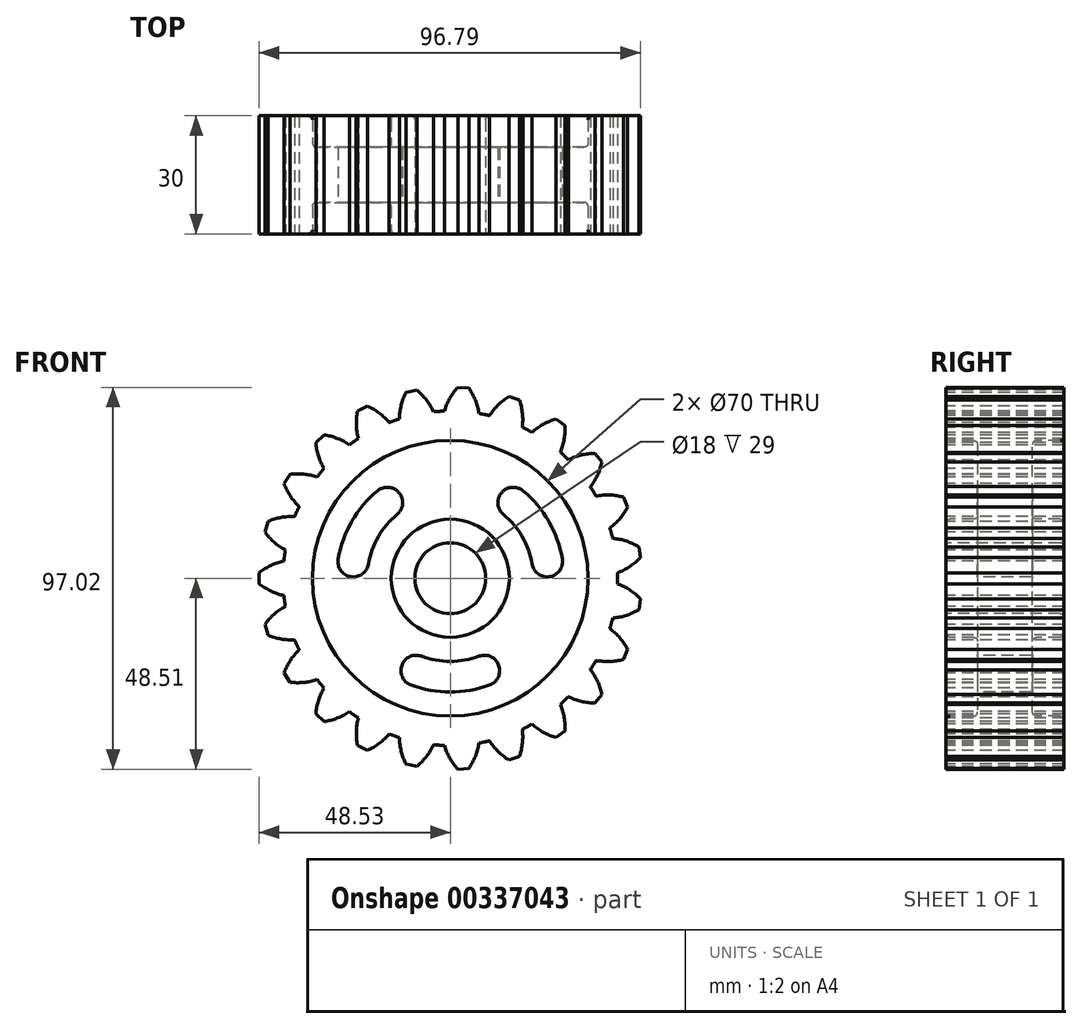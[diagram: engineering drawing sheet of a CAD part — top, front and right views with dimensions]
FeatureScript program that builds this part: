
annotation { "Feature Type Name" : "Feature", "Feature Type Description" : "" }
export const myFeature = defineFeature(function(context is Context, id is Id, definition is map)
    precondition{}
    {
        {
            var Q0;
            Q0=qCreatedBy(makeId("Right.planeOp"),FACE);
            var sketch = newSketch(context, id + "F0", { "sketchPlane" : qUnion([Q0])});
            skLineSegment(sketch, "E0", {"start": v(-15, 0) * mm, "end": v(15, 0) * mm});
            skLineSegment(sketch, "E1", {"start": v(15, 0) * mm, "end": v(15, 15) * mm});
            skLineSegment(sketch, "E2", {"start": v(15, 15) * mm, "end": v(7, 15) * mm});
            skLineSegment(sketch, "E3", {"start": v(7, 15) * mm, "end": v(7, 35) * mm});
            skLineSegment(sketch, "E4", {"start": v(7, 35) * mm, "end": v(15, 35) * mm});
            skLineSegment(sketch, "E5", {"start": v(15, 35) * mm, "end": v(15, 42.5) * mm});
            skLineSegment(sketch, "E6", {"start": v(15, 42.5) * mm, "end": v(-15, 42.5) * mm});
            skLineSegment(sketch, "E7", {"start": v(-15, 42.5) * mm, "end": v(-15, 35) * mm});
            skLineSegment(sketch, "E8", {"start": v(-15, 35) * mm, "end": v(-7, 35) * mm});
            skLineSegment(sketch, "E9", {"start": v(-7, 35) * mm, "end": v(-7, 15) * mm});
            skLineSegment(sketch, "E10", {"start": v(-7, 15) * mm, "end": v(-15, 15) * mm});
            skLineSegment(sketch, "E11", {"start": v(-15, 15) * mm, "end": v(-15, 0) * mm});
            skSolve(sketch);
        }
        {
            var Q0;
            Q0=makeQuery(id+"F0.imprint","IMPRINT",FACE,{"disambiguationData":[TD([[makeQuery(id+"F0.imprint","IMPRINT",EDGE,{"derivedFrom":sQuery(id+"F0.wireOp",EDGE,"E0")}),1.0]])]});
            var Q1;
            Q1=sQuery(id+"F0.wireOp",EDGE,"E0");
            revolve(context, id + "F1", {"entities" : qUnion([Q0]), "axis" : qUnion([Q1]), "revolveType" : RevolveType.FULL});
        }
        {
            var Q0;
            Q0=makeQuery(id+"F1.opRevolve","SWEPT_FACE",FACE,{"disambiguationData":[OSD([sQuery(id+"F0.wireOp",EDGE,"E11")])]});
            var sketch = newSketch(context, id + "F2", { "sketchPlane" : qUnion([Q0])});
            skCircle(sketch, "E12", {"center": v(0, 0) * mm, "radius": 9 * mm});
            skSolve(sketch);
        }
        {
            var Q0;
            Q0=makeQuery(id+"F2.imprint","IMPRINT",FACE,{"disambiguationData":[TD([[makeQuery(id+"F2.imprint","IMPRINT",EDGE,{"derivedFrom":sQuery(id+"F2.wireOp",EDGE,"E12")}),1.0]])]});
            extrude(context, id + "F3", {"entities" : qUnion([Q0]), "operationType" : NewBodyOperationType.REMOVE, "oppositeDirection" : true, "depth" : 35.8 * mm});
        }
        {
            var Q0;
            Q0=makeQuery(id+"F1.opRevolve","SWEPT_FACE",FACE,{"disambiguationData":[OSD([sQuery(id+"F0.wireOp",EDGE,"E7")])]});
            var sketch = newSketch(context, id + "F4", { "sketchPlane" : qUnion([Q0])});
            skLineSegment(sketch, "E13", {"start": v(0, 0) * mm, "end": v(-48.53, 0) * mm, "construction": true});
            skLineSegment(sketch, "E14", {"start": v(-48.53, 0) * mm, "end": v(-48.53, 1.4) * mm});
            skArc(sketch, "E15", {"start": v(-42.27, 4.4) * mm, "mid": v(-45.57, 3.27) * mm, "end": v(-48.53, 1.4) * mm});
            skLineSegment(sketch, "E16.MirrorCS", {"start": v(-48.53, 0) * mm, "end": v(-48.53, -1.4) * mm});
            skArc(sketch, "E17.MirrorCS", {"start": v(-42.27, -4.4) * mm, "mid": v(-45.57, -3.27) * mm, "end": v(-48.53, -1.4) * mm});
            skLineSegment(sketch, "E18.1.0", {"start": v(-46.73, -13.1) * mm, "end": v(-47.1, -11.74) * mm});
            skArc(sketch, "E18.1.1", {"start": v(-41.9, -7.17) * mm, "mid": v(-44.77, -9.15) * mm, "end": v(-47.1, -11.74) * mm});
            skLineSegment(sketch, "E18.1.2", {"start": v(-46.73, -13.1) * mm, "end": v(-46.35, -14.44) * mm});
            skArc(sketch, "E18.1.3", {"start": v(-39.52, -15.64) * mm, "mid": v(-43, -15.44) * mm, "end": v(-46.35, -14.44) * mm});
            skLineSegment(sketch, "E18.2.0", {"start": v(-41.46, -25.21) * mm, "end": v(-42.19, -24.02) * mm});
            skArc(sketch, "E18.2.1", {"start": v(-38.4, -18.2) * mm, "mid": v(-40.64, -20.89) * mm, "end": v(-42.19, -24.02) * mm});
            skLineSegment(sketch, "E18.2.2", {"start": v(-41.46, -25.21) * mm, "end": v(-40.73, -26.4) * mm});
            skArc(sketch, "E18.2.3", {"start": v(-33.83, -25.72) * mm, "mid": v(-37.24, -26.47) * mm, "end": v(-40.73, -26.4) * mm});
            skLineSegment(sketch, "E18.3.0", {"start": v(-33.12, -35.46) * mm, "end": v(-34.14, -34.5) * mm});
            skArc(sketch, "E18.3.1", {"start": v(-32.07, -27.9) * mm, "mid": v(-33.5, -31.08) * mm, "end": v(-34.14, -34.5) * mm});
            skLineSegment(sketch, "E18.3.2", {"start": v(-33.12, -35.46) * mm, "end": v(-32.1, -36.42) * mm});
            skArc(sketch, "E18.3.3", {"start": v(-25.64, -33.9) * mm, "mid": v(-28.72, -35.54) * mm, "end": v(-32.1, -36.42) * mm});
            skLineSegment(sketch, "E18.4.0", {"start": v(-22.33, -43.09) * mm, "end": v(-23.57, -42.44) * mm});
            skArc(sketch, "E18.4.1", {"start": v(-23.35, -35.5) * mm, "mid": v(-23.87, -38.96) * mm, "end": v(-23.57, -42.44) * mm});
            skLineSegment(sketch, "E18.4.2", {"start": v(-22.33, -43.09) * mm, "end": v(-21.08, -43.73) * mm});
            skArc(sketch, "E18.4.3", {"start": v(-15.54, -39.56) * mm, "mid": v(-18.07, -41.97) * mm, "end": v(-21.08, -43.73) * mm});
            skLineSegment(sketch, "E18.5.0", {"start": v(-9.87, -47.51) * mm, "end": v(-11.24, -47.23) * mm});
            skArc(sketch, "E18.5.1", {"start": v(-12.9, -40.5) * mm, "mid": v(-12.47, -43.96) * mm, "end": v(-11.24, -47.23) * mm});
            skLineSegment(sketch, "E18.5.2", {"start": v(-9.87, -47.51) * mm, "end": v(-8.5, -47.8) * mm});
            skArc(sketch, "E18.5.3", {"start": v(-4.3, -42.28) * mm, "mid": v(-6.07, -45.29) * mm, "end": v(-8.5, -47.8) * mm});
            skLineSegment(sketch, "E18.6.0", {"start": v(3.31, -48.41) * mm, "end": v(1.91, -48.5) * mm});
            skArc(sketch, "E18.6.1", {"start": v(-1.5, -42.47) * mm, "mid": v(-0.15, -45.7) * mm, "end": v(1.91, -48.5) * mm});
            skLineSegment(sketch, "E18.6.2", {"start": v(3.31, -48.41) * mm, "end": v(4.7, -48.32) * mm});
            skArc(sketch, "E18.6.3", {"start": v(7.27, -41.87) * mm, "mid": v(6.37, -45.25) * mm, "end": v(4.7, -48.32) * mm});
            skLineSegment(sketch, "E18.7.0", {"start": v(16.25, -45.72) * mm, "end": v(14.93, -46.2) * mm});
            skArc(sketch, "E18.7.1", {"start": v(10, -41.3) * mm, "mid": v(12.18, -44.04) * mm, "end": v(14.93, -46.2) * mm});
            skLineSegment(sketch, "E18.7.2", {"start": v(16.25, -45.72) * mm, "end": v(17.57, -45.26) * mm});
            skArc(sketch, "E18.7.3", {"start": v(18.3, -38.36) * mm, "mid": v(18.34, -41.85) * mm, "end": v(17.57, -45.26) * mm});
            skLineSegment(sketch, "E18.8.0", {"start": v(27.98, -39.64) * mm, "end": v(26.84, -40.45) * mm});
            skArc(sketch, "E18.8.1", {"start": v(20.78, -37.07) * mm, "mid": v(23.61, -39.12) * mm, "end": v(26.84, -40.45) * mm});
            skLineSegment(sketch, "E18.8.2", {"start": v(27.98, -39.64) * mm, "end": v(29.13, -38.84) * mm});
            skArc(sketch, "E18.8.3", {"start": v(27.97, -32) * mm, "mid": v(28.95, -35.35) * mm, "end": v(29.13, -38.84) * mm});
            skLineSegment(sketch, "E18.9.0", {"start": v(37.64, -30.62) * mm, "end": v(36.76, -31.71) * mm});
            skArc(sketch, "E18.9.1", {"start": v(30.01, -30.1) * mm, "mid": v(33.3, -31.3) * mm, "end": v(36.76, -31.71) * mm});
            skLineSegment(sketch, "E18.9.2", {"start": v(37.64, -30.62) * mm, "end": v(38.53, -29.54) * mm});
            skArc(sketch, "E18.9.3", {"start": v(35.57, -23.26) * mm, "mid": v(37.41, -26.23) * mm, "end": v(38.53, -29.54) * mm});
            skLineSegment(sketch, "E18.10.0", {"start": v(44.5, -19.33) * mm, "end": v(43.95, -20.62) * mm});
            skArc(sketch, "E18.10.1", {"start": v(37.02, -20.88) * mm, "mid": v(40.5, -21.15) * mm, "end": v(43.95, -20.62) * mm});
            skLineSegment(sketch, "E18.10.2", {"start": v(44.5, -19.33) * mm, "end": v(45.07, -18.05) * mm});
            skArc(sketch, "E18.10.3", {"start": v(40.52, -12.8) * mm, "mid": v(43.1, -15.16) * mm, "end": v(45.07, -18.05) * mm});
            skLineSegment(sketch, "E18.11.0", {"start": v(48.07, -6.6) * mm, "end": v(47.88, -8) * mm});
            skArc(sketch, "E18.11.1", {"start": v(41.28, -10.12) * mm, "mid": v(44.7, -9.44) * mm, "end": v(47.88, -8) * mm});
            skLineSegment(sketch, "E18.11.2", {"start": v(48.07, -6.6) * mm, "end": v(48.26, -5.22) * mm});
            skArc(sketch, "E18.11.3", {"start": v(42.48, -1.4) * mm, "mid": v(45.6, -2.97) * mm, "end": v(48.26, -5.22) * mm});
            skLineSegment(sketch, "E18.12.0", {"start": v(48.07, 6.6) * mm, "end": v(48.26, 5.22) * mm});
            skArc(sketch, "E18.12.1", {"start": v(42.48, 1.4) * mm, "mid": v(45.6, 2.97) * mm, "end": v(48.26, 5.22) * mm});
            skLineSegment(sketch, "E18.12.2", {"start": v(48.07, 6.6) * mm, "end": v(47.88, 8) * mm});
            skArc(sketch, "E18.12.3", {"start": v(41.28, 10.12) * mm, "mid": v(44.7, 9.44) * mm, "end": v(47.88, 8) * mm});
            skLineSegment(sketch, "E18.13.0", {"start": v(44.5, 19.33) * mm, "end": v(45.07, 18.05) * mm});
            skArc(sketch, "E18.13.1", {"start": v(40.52, 12.8) * mm, "mid": v(43.1, 15.16) * mm, "end": v(45.07, 18.05) * mm});
            skLineSegment(sketch, "E18.13.2", {"start": v(44.5, 19.33) * mm, "end": v(43.95, 20.62) * mm});
            skArc(sketch, "E18.13.3", {"start": v(37.02, 20.88) * mm, "mid": v(40.5, 21.15) * mm, "end": v(43.95, 20.62) * mm});
            skLineSegment(sketch, "E18.14.0", {"start": v(37.64, 30.62) * mm, "end": v(38.53, 29.54) * mm});
            skArc(sketch, "E18.14.1", {"start": v(35.57, 23.26) * mm, "mid": v(37.41, 26.23) * mm, "end": v(38.53, 29.54) * mm});
            skLineSegment(sketch, "E18.14.2", {"start": v(37.64, 30.62) * mm, "end": v(36.76, 31.71) * mm});
            skArc(sketch, "E18.14.3", {"start": v(30.01, 30.1) * mm, "mid": v(33.3, 31.3) * mm, "end": v(36.76, 31.71) * mm});
            skLineSegment(sketch, "E18.15.0", {"start": v(27.98, 39.64) * mm, "end": v(29.13, 38.84) * mm});
            skArc(sketch, "E18.15.1", {"start": v(27.97, 32) * mm, "mid": v(28.95, 35.35) * mm, "end": v(29.13, 38.84) * mm});
            skLineSegment(sketch, "E18.15.2", {"start": v(27.98, 39.64) * mm, "end": v(26.84, 40.45) * mm});
            skArc(sketch, "E18.15.3", {"start": v(20.78, 37.07) * mm, "mid": v(23.61, 39.12) * mm, "end": v(26.84, 40.45) * mm});
            skLineSegment(sketch, "E18.16.0", {"start": v(16.25, 45.72) * mm, "end": v(17.57, 45.26) * mm});
            skArc(sketch, "E18.16.1", {"start": v(18.3, 38.36) * mm, "mid": v(18.34, 41.85) * mm, "end": v(17.57, 45.26) * mm});
            skLineSegment(sketch, "E18.16.2", {"start": v(16.25, 45.72) * mm, "end": v(14.93, 46.2) * mm});
            skArc(sketch, "E18.16.3", {"start": v(10, 41.3) * mm, "mid": v(12.18, 44.04) * mm, "end": v(14.93, 46.2) * mm});
            skLineSegment(sketch, "E18.17.0", {"start": v(3.31, 48.41) * mm, "end": v(4.7, 48.32) * mm});
            skArc(sketch, "E18.17.1", {"start": v(7.27, 41.87) * mm, "mid": v(6.37, 45.25) * mm, "end": v(4.7, 48.32) * mm});
            skLineSegment(sketch, "E18.17.2", {"start": v(3.31, 48.41) * mm, "end": v(1.91, 48.5) * mm});
            skArc(sketch, "E18.17.3", {"start": v(-1.5, 42.47) * mm, "mid": v(-0.15, 45.7) * mm, "end": v(1.91, 48.5) * mm});
            skLineSegment(sketch, "E18.18.0", {"start": v(-9.87, 47.51) * mm, "end": v(-8.5, 47.8) * mm});
            skArc(sketch, "E18.18.1", {"start": v(-4.3, 42.28) * mm, "mid": v(-6.07, 45.29) * mm, "end": v(-8.5, 47.8) * mm});
            skLineSegment(sketch, "E18.18.2", {"start": v(-9.87, 47.51) * mm, "end": v(-11.24, 47.23) * mm});
            skArc(sketch, "E18.18.3", {"start": v(-12.9, 40.5) * mm, "mid": v(-12.47, 43.96) * mm, "end": v(-11.24, 47.23) * mm});
            skLineSegment(sketch, "E18.19.0", {"start": v(-22.33, 43.09) * mm, "end": v(-21.08, 43.73) * mm});
            skArc(sketch, "E18.19.1", {"start": v(-15.54, 39.56) * mm, "mid": v(-18.07, 41.97) * mm, "end": v(-21.08, 43.73) * mm});
            skLineSegment(sketch, "E18.19.2", {"start": v(-22.33, 43.09) * mm, "end": v(-23.57, 42.44) * mm});
            skArc(sketch, "E18.19.3", {"start": v(-23.35, 35.5) * mm, "mid": v(-23.87, 38.96) * mm, "end": v(-23.57, 42.44) * mm});
            skLineSegment(sketch, "E18.20.0", {"start": v(-33.12, 35.46) * mm, "end": v(-32.1, 36.42) * mm});
            skArc(sketch, "E18.20.1", {"start": v(-25.64, 33.9) * mm, "mid": v(-28.72, 35.54) * mm, "end": v(-32.1, 36.42) * mm});
            skLineSegment(sketch, "E18.20.2", {"start": v(-33.12, 35.46) * mm, "end": v(-34.14, 34.5) * mm});
            skArc(sketch, "E18.20.3", {"start": v(-32.07, 27.9) * mm, "mid": v(-33.5, 31.08) * mm, "end": v(-34.14, 34.5) * mm});
            skLineSegment(sketch, "E18.21.0", {"start": v(-41.46, 25.21) * mm, "end": v(-40.73, 26.4) * mm});
            skArc(sketch, "E18.21.1", {"start": v(-33.83, 25.72) * mm, "mid": v(-37.24, 26.47) * mm, "end": v(-40.73, 26.4) * mm});
            skLineSegment(sketch, "E18.21.2", {"start": v(-41.46, 25.21) * mm, "end": v(-42.19, 24.02) * mm});
            skArc(sketch, "E18.21.3", {"start": v(-38.4, 18.2) * mm, "mid": v(-40.64, 20.89) * mm, "end": v(-42.19, 24.02) * mm});
            skLineSegment(sketch, "E18.22.0", {"start": v(-46.73, 13.1) * mm, "end": v(-46.35, 14.44) * mm});
            skArc(sketch, "E18.22.1", {"start": v(-39.52, 15.64) * mm, "mid": v(-43, 15.44) * mm, "end": v(-46.35, 14.44) * mm});
            skLineSegment(sketch, "E18.22.2", {"start": v(-46.73, 13.1) * mm, "end": v(-47.1, 11.74) * mm});
            skArc(sketch, "E18.22.3", {"start": v(-41.9, 7.17) * mm, "mid": v(-44.77, 9.15) * mm, "end": v(-47.1, 11.74) * mm});
            skPoint(sketch, "E18.center", {"position": v(0, 0) * mm});
            skSolve(sketch);
        }
        {
            var Q0;
            Q0=makeQuery(id+"F4.imprint","IMPRINT",FACE,{"disambiguationData":[TD([[makeQuery(id+"F4.imprint","IMPRINT",EDGE,{"derivedFrom":sQuery(id+"F4.wireOp",EDGE,"E18.1.0")}),-1.0]])]});
            var Q1;
            Q1=makeQuery(id+"F4.imprint","IMPRINT",FACE,{"disambiguationData":[TD([[makeQuery(id+"F4.imprint","IMPRINT",EDGE,{"derivedFrom":sQuery(id+"F4.wireOp",EDGE,"E14")}),-1.0]])]});
            var Q2;
            Q2=makeQuery(id+"F4.imprint","IMPRINT",FACE,{"disambiguationData":[TD([[makeQuery(id+"F4.imprint","IMPRINT",EDGE,{"derivedFrom":sQuery(id+"F4.wireOp",EDGE,"E18.22.0")}),-1.0]])]});
            var Q3;
            Q3=makeQuery(id+"F4.imprint","IMPRINT",FACE,{"disambiguationData":[TD([[makeQuery(id+"F4.imprint","IMPRINT",EDGE,{"derivedFrom":sQuery(id+"F4.wireOp",EDGE,"E18.21.0")}),-1.0]])]});
            var Q4;
            Q4=makeQuery(id+"F4.imprint","IMPRINT",FACE,{"disambiguationData":[TD([[makeQuery(id+"F4.imprint","IMPRINT",EDGE,{"derivedFrom":sQuery(id+"F4.wireOp",EDGE,"E18.20.0")}),-1.0]])]});
            var Q5;
            Q5=makeQuery(id+"F4.imprint","IMPRINT",FACE,{"disambiguationData":[TD([[makeQuery(id+"F4.imprint","IMPRINT",EDGE,{"derivedFrom":sQuery(id+"F4.wireOp",EDGE,"E18.19.0")}),-1.0]])]});
            var Q6;
            Q6=makeQuery(id+"F4.imprint","IMPRINT",FACE,{"disambiguationData":[TD([[makeQuery(id+"F4.imprint","IMPRINT",EDGE,{"derivedFrom":sQuery(id+"F4.wireOp",EDGE,"E18.18.0")}),-1.0]])]});
            var Q7;
            Q7=makeQuery(id+"F4.imprint","IMPRINT",FACE,{"disambiguationData":[TD([[makeQuery(id+"F4.imprint","IMPRINT",EDGE,{"derivedFrom":sQuery(id+"F4.wireOp",EDGE,"E18.17.0")}),-1.0]])]});
            var Q8;
            Q8=makeQuery(id+"F4.imprint","IMPRINT",FACE,{"disambiguationData":[TD([[makeQuery(id+"F4.imprint","IMPRINT",EDGE,{"derivedFrom":sQuery(id+"F4.wireOp",EDGE,"E18.16.0")}),-1.0]])]});
            var Q9;
            Q9=makeQuery(id+"F4.imprint","IMPRINT",FACE,{"disambiguationData":[TD([[makeQuery(id+"F4.imprint","IMPRINT",EDGE,{"derivedFrom":sQuery(id+"F4.wireOp",EDGE,"E18.15.0")}),-1.0]])]});
            var Q10;
            Q10=makeQuery(id+"F4.imprint","IMPRINT",FACE,{"disambiguationData":[TD([[makeQuery(id+"F4.imprint","IMPRINT",EDGE,{"derivedFrom":sQuery(id+"F4.wireOp",EDGE,"E18.14.0")}),-1.0]])]});
            var Q11;
            Q11=makeQuery(id+"F4.imprint","IMPRINT",FACE,{"disambiguationData":[TD([[makeQuery(id+"F4.imprint","IMPRINT",EDGE,{"derivedFrom":sQuery(id+"F4.wireOp",EDGE,"E18.13.0")}),-1.0]])]});
            var Q12;
            Q12=makeQuery(id+"F4.imprint","IMPRINT",FACE,{"disambiguationData":[TD([[makeQuery(id+"F4.imprint","IMPRINT",EDGE,{"derivedFrom":sQuery(id+"F4.wireOp",EDGE,"E18.12.0")}),-1.0]])]});
            var Q13;
            Q13=makeQuery(id+"F4.imprint","IMPRINT",FACE,{"disambiguationData":[TD([[makeQuery(id+"F4.imprint","IMPRINT",EDGE,{"derivedFrom":sQuery(id+"F4.wireOp",EDGE,"E18.11.0")}),-1.0]])]});
            var Q14;
            Q14=makeQuery(id+"F4.imprint","IMPRINT",FACE,{"disambiguationData":[TD([[makeQuery(id+"F4.imprint","IMPRINT",EDGE,{"derivedFrom":sQuery(id+"F4.wireOp",EDGE,"E18.10.0")}),-1.0]])]});
            var Q15;
            Q15=makeQuery(id+"F4.imprint","IMPRINT",FACE,{"disambiguationData":[TD([[makeQuery(id+"F4.imprint","IMPRINT",EDGE,{"derivedFrom":sQuery(id+"F4.wireOp",EDGE,"E18.9.0")}),-1.0]])]});
            var Q16;
            Q16=makeQuery(id+"F4.imprint","IMPRINT",FACE,{"disambiguationData":[TD([[makeQuery(id+"F4.imprint","IMPRINT",EDGE,{"derivedFrom":sQuery(id+"F4.wireOp",EDGE,"E18.8.0")}),-1.0]])]});
            var Q17;
            Q17=makeQuery(id+"F4.imprint","IMPRINT",FACE,{"disambiguationData":[TD([[makeQuery(id+"F4.imprint","IMPRINT",EDGE,{"derivedFrom":sQuery(id+"F4.wireOp",EDGE,"E18.7.0")}),-1.0]])]});
            var Q18;
            Q18=makeQuery(id+"F4.imprint","IMPRINT",FACE,{"disambiguationData":[TD([[makeQuery(id+"F4.imprint","IMPRINT",EDGE,{"derivedFrom":sQuery(id+"F4.wireOp",EDGE,"E18.6.0")}),-1.0]])]});
            var Q19;
            Q19=makeQuery(id+"F4.imprint","IMPRINT",FACE,{"disambiguationData":[TD([[makeQuery(id+"F4.imprint","IMPRINT",EDGE,{"derivedFrom":sQuery(id+"F4.wireOp",EDGE,"E18.5.0")}),-1.0]])]});
            var Q20;
            Q20=makeQuery(id+"F4.imprint","IMPRINT",FACE,{"disambiguationData":[TD([[makeQuery(id+"F4.imprint","IMPRINT",EDGE,{"derivedFrom":sQuery(id+"F4.wireOp",EDGE,"E18.4.0")}),-1.0]])]});
            var Q21;
            Q21=makeQuery(id+"F4.imprint","IMPRINT",FACE,{"disambiguationData":[TD([[makeQuery(id+"F4.imprint","IMPRINT",EDGE,{"derivedFrom":sQuery(id+"F4.wireOp",EDGE,"E18.5.0")}),-1.0]])]});
            var Q22;
            Q22=makeQuery(id+"F4.imprint","IMPRINT",FACE,{"disambiguationData":[TD([[makeQuery(id+"F4.imprint","IMPRINT",EDGE,{"derivedFrom":sQuery(id+"F4.wireOp",EDGE,"E18.3.0")}),-1.0]])]});
            var Q23;
            Q23=makeQuery(id+"F4.imprint","IMPRINT",FACE,{"disambiguationData":[TD([[makeQuery(id+"F4.imprint","IMPRINT",EDGE,{"derivedFrom":sQuery(id+"F4.wireOp",EDGE,"E18.2.0")}),-1.0]])]});
            var Q24;
            Q24=makeQuery(id+"F1.opRevolve","SWEPT_FACE",FACE,{"disambiguationData":[OSD([sQuery(id+"F0.wireOp",EDGE,"E5")])]});
            extrude(context, id + "F5", {"entities" : qUnion([Q0, Q1, Q2, Q3, Q4, Q5, Q6, Q7, Q8, Q9, Q10, Q11, Q12, Q13, Q14, Q15, Q16, Q17, Q18, Q19, Q20, Q21, Q22, Q23]), "operationType" : NewBodyOperationType.ADD, "endBound" : BoundingType.UP_TO_SURFACE, "oppositeDirection" : true, "endBoundEntityFace" : qUnion([Q24]), "depth" : 25 * mm});
        }
        {
            var Q0;
            Q0=makeQuery(id+"F1.opRevolve","SWEPT_FACE",FACE,{"disambiguationData":[OSD([sQuery(id+"F0.wireOp",EDGE,"E9")])]});
            var sketch = newSketch(context, id + "F6", { "sketchPlane" : qUnion([Q0])});
            skArc(sketch, "E19", {"start": v(-10, -27.11) * mm, "mid": v(0, -28.9) * mm, "end": v(10, -27.11) * mm});
            skArc(sketch, "E20", {"start": v(-7.3, -19.8) * mm, "mid": v(0, -21.1) * mm, "end": v(7.3, -19.8) * mm});
            skLineSegment(sketch, "E21", {"start": v(0, 0) * mm, "end": v(-10, -27.11) * mm, "construction": true});
            skLineSegment(sketch, "E22", {"start": v(0, 0) * mm, "end": v(10, -27.11) * mm, "construction": true});
            skArc(sketch, "E23", {"start": v(-7.3, -19.8) * mm, "mid": v(-12.3, -22.1) * mm, "end": v(-10, -27.11) * mm});
            skArc(sketch, "E24", {"start": v(10, -27.11) * mm, "mid": v(12.3, -22.1) * mm, "end": v(7.3, -19.8) * mm});
            skArc(sketch, "E25.1.0", {"start": v(20.8, 3.58) * mm, "mid": v(18.27, 10.55) * mm, "end": v(13.5, 16.22) * mm});
            skArc(sketch, "E25.1.1", {"start": v(18.48, 22.22) * mm, "mid": v(12.99, 21.71) * mm, "end": v(13.5, 16.22) * mm});
            skArc(sketch, "E25.1.2", {"start": v(28.48, 4.9) * mm, "mid": v(25.03, 14.45) * mm, "end": v(18.48, 22.22) * mm});
            skArc(sketch, "E25.1.3", {"start": v(20.8, 3.58) * mm, "mid": v(25.3, 0.4) * mm, "end": v(28.48, 4.9) * mm});
            skArc(sketch, "E25.2.0", {"start": v(-13.5, 16.22) * mm, "mid": v(-18.27, 10.55) * mm, "end": v(-20.8, 3.58) * mm});
            skArc(sketch, "E25.2.1", {"start": v(-28.48, 4.9) * mm, "mid": v(-25.3, 0.4) * mm, "end": v(-20.8, 3.58) * mm});
            skArc(sketch, "E25.2.2", {"start": v(-18.48, 22.22) * mm, "mid": v(-25.03, 14.45) * mm, "end": v(-28.48, 4.9) * mm});
            skArc(sketch, "E25.2.3", {"start": v(-13.5, 16.22) * mm, "mid": v(-12.99, 21.71) * mm, "end": v(-18.48, 22.22) * mm});
            skSolve(sketch);
        }
        {
            var Q0;
            Q0=makeQuery(id+"F6.imprint","IMPRINT",FACE,{"disambiguationData":[TD([[makeQuery(id+"F6.imprint","IMPRINT",EDGE,{"derivedFrom":sQuery(id+"F6.wireOp",EDGE,"E25.2.0")}),-1.0]])]});
            var Q1;
            Q1=makeQuery(id+"F6.imprint","IMPRINT",FACE,{"disambiguationData":[TD([[makeQuery(id+"F6.imprint","IMPRINT",EDGE,{"derivedFrom":sQuery(id+"F6.wireOp",EDGE,"E25.1.0")}),-1.0]])]});
            var Q2;
            Q2=makeQuery(id+"F6.imprint","IMPRINT",FACE,{"disambiguationData":[TD([[makeQuery(id+"F6.imprint","IMPRINT",EDGE,{"derivedFrom":sQuery(id+"F6.wireOp",EDGE,"E19")}),1.0]])]});
            extrude(context, id + "F7", {"entities" : qUnion([Q0, Q1, Q2]), "operationType" : NewBodyOperationType.REMOVE, "oppositeDirection" : true, "depth" : 25 * mm});
        }
        {
            var Q0;
            Q0=makeQuery(id+"F1.opRevolve","SWEPT_EDGE",EDGE,{"disambiguationData":[OSD([sQuery(id+"F0.wireOp",EDGE,"E8"),sQuery(id+"F0.wireOp",EDGE,"E9")])]});
            var Q1;
            Q1=makeQuery(id+"F1.opRevolve","SWEPT_EDGE",EDGE,{"disambiguationData":[OSD([sQuery(id+"F0.wireOp",EDGE,"E7"),sQuery(id+"F0.wireOp",EDGE,"E8")])]});
            var Q2;
            Q2=makeQuery(id+"F1.opRevolve","SWEPT_EDGE",EDGE,{"disambiguationData":[OSD([sQuery(id+"F0.wireOp",EDGE,"E9"),sQuery(id+"F0.wireOp",EDGE,"E10")])]});
            var Q3;
            Q3=makeQuery(id+"F1.opRevolve","SWEPT_EDGE",EDGE,{"disambiguationData":[OSD([sQuery(id+"F0.wireOp",EDGE,"E3"),sQuery(id+"F0.wireOp",EDGE,"E4")])]});
            var Q4;
            Q4=makeQuery(id+"F1.opRevolve","SWEPT_EDGE",EDGE,{"disambiguationData":[OSD([sQuery(id+"F0.wireOp",EDGE,"E4"),sQuery(id+"F0.wireOp",EDGE,"E5")])]});
            var Q5;
            Q5=makeQuery(id+"F1.opRevolve","SWEPT_EDGE",EDGE,{"disambiguationData":[OSD([sQuery(id+"F0.wireOp",EDGE,"E2"),sQuery(id+"F0.wireOp",EDGE,"E3")])]});
            var Q6;
            Q6=makeQuery(id+"F3.boolean.opBoolean","INTERSECT",EDGE,{"derivedFrom":[makeQuery(id+"F1.opRevolve","SWEPT_FACE",FACE,{"disambiguationData":[OSD([sQuery(id+"F0.wireOp",EDGE,"E1")])]}),makeQuery(id+"F3.opExtrude","SWEPT_FACE",FACE,{"disambiguationData":[OSD([sQuery(id+"F2.wireOp",EDGE,"E12")])]})]});
            var Q7;
            Q7=makeQuery(id+"F1.opRevolve","SWEPT_EDGE",EDGE,{"disambiguationData":[OSD([sQuery(id+"F0.wireOp",EDGE,"E1"),sQuery(id+"F0.wireOp",EDGE,"E2")])]});
            fillet(context, id + "F8", {"entities" : qUnion([Q0, Q1, Q2, Q3, Q4, Q5, Q6, Q7]), "radius" : 1 * mm, "tangentPropagation" : true, "allowEdgeOverflow" : false});
        }
        {
            var Q0;
            Q0=makeQuery(id+"F1.opRevolve","SWEPT_EDGE",EDGE,{"disambiguationData":[OSD([sQuery(id+"F0.wireOp",EDGE,"E10"),sQuery(id+"F0.wireOp",EDGE,"E11")])]});
            fillet(context, id + "F9", {"entities" : qUnion([Q0]), "radius" : 1 * mm, "tangentPropagation" : true, "allowEdgeOverflow" : false});
        }
        {
            var Q0;
            Q0=makeQuery(id+"F7.boolean.opBoolean","COPY",EDGE,{"derivedFrom":makeQuery(id+"F7.opExtrude","CAP_EDGE",EDGE,{"disambiguationData":[OSD([sQuery(id+"F6.wireOp",EDGE,"E25.1.2")])],"isStart":true})});
            var Q1;
            Q1=makeQuery(id+"F7.boolean.opBoolean","COPY",EDGE,{"derivedFrom":makeQuery(id+"F7.opExtrude","CAP_EDGE",EDGE,{"disambiguationData":[OSD([sQuery(id+"F6.wireOp",EDGE,"E25.1.0")])],"isStart":true})});
            var Q2;
            Q2=makeQuery(id+"F7.boolean.opBoolean","COPY",EDGE,{"derivedFrom":makeQuery(id+"F7.opExtrude","CAP_EDGE",EDGE,{"disambiguationData":[OSD([sQuery(id+"F6.wireOp",EDGE,"E20")])],"isStart":true})});
            var Q3;
            Q3=makeQuery(id+"F7.boolean.opBoolean","COPY",EDGE,{"derivedFrom":makeQuery(id+"F7.opExtrude","CAP_EDGE",EDGE,{"disambiguationData":[OSD([sQuery(id+"F6.wireOp",EDGE,"E19")])],"isStart":true})});
            var Q4;
            Q4=makeQuery(id+"F7.boolean.opBoolean","COPY",EDGE,{"derivedFrom":makeQuery(id+"F7.opExtrude","CAP_EDGE",EDGE,{"disambiguationData":[OSD([sQuery(id+"F6.wireOp",EDGE,"E25.2.0")])],"isStart":true})});
            var Q5;
            Q5=makeQuery(id+"F7.boolean.opBoolean","COPY",EDGE,{"derivedFrom":makeQuery(id+"F7.opExtrude","CAP_EDGE",EDGE,{"disambiguationData":[OSD([sQuery(id+"F6.wireOp",EDGE,"E25.2.2")])],"isStart":true})});
            var Q6;
            Q6=makeQuery(id+"F7.boolean.opBoolean","INTERSECT",EDGE,{"derivedFrom":[makeQuery(id+"F1.opRevolve","SWEPT_FACE",FACE,{"disambiguationData":[OSD([sQuery(id+"F0.wireOp",EDGE,"E3")])]}),makeQuery(id+"F7.opExtrude","SWEPT_FACE",FACE,{"disambiguationData":[OSD([sQuery(id+"F6.wireOp",EDGE,"E25.1.0")])]})]});
            var Q7;
            Q7=makeQuery(id+"F7.boolean.opBoolean","INTERSECT",EDGE,{"derivedFrom":[makeQuery(id+"F1.opRevolve","SWEPT_FACE",FACE,{"disambiguationData":[OSD([sQuery(id+"F0.wireOp",EDGE,"E3")])]}),makeQuery(id+"F7.opExtrude","SWEPT_FACE",FACE,{"disambiguationData":[OSD([sQuery(id+"F6.wireOp",EDGE,"E25.1.2")])]})]});
            var Q8;
            Q8=makeQuery(id+"F7.boolean.opBoolean","INTERSECT",EDGE,{"derivedFrom":[makeQuery(id+"F1.opRevolve","SWEPT_FACE",FACE,{"disambiguationData":[OSD([sQuery(id+"F0.wireOp",EDGE,"E3")])]}),makeQuery(id+"F7.opExtrude","SWEPT_FACE",FACE,{"disambiguationData":[OSD([sQuery(id+"F6.wireOp",EDGE,"E20")])]})]});
            var Q9;
            Q9=makeQuery(id+"F7.boolean.opBoolean","INTERSECT",EDGE,{"derivedFrom":[makeQuery(id+"F1.opRevolve","SWEPT_FACE",FACE,{"disambiguationData":[OSD([sQuery(id+"F0.wireOp",EDGE,"E3")])]}),makeQuery(id+"F7.opExtrude","SWEPT_FACE",FACE,{"disambiguationData":[OSD([sQuery(id+"F6.wireOp",EDGE,"E19")])]})]});
            var Q10;
            Q10=makeQuery(id+"F7.boolean.opBoolean","INTERSECT",EDGE,{"derivedFrom":[makeQuery(id+"F1.opRevolve","SWEPT_FACE",FACE,{"disambiguationData":[OSD([sQuery(id+"F0.wireOp",EDGE,"E3")])]}),makeQuery(id+"F7.opExtrude","SWEPT_FACE",FACE,{"disambiguationData":[OSD([sQuery(id+"F6.wireOp",EDGE,"E25.2.0")])]})]});
            var Q11;
            Q11=makeQuery(id+"F7.boolean.opBoolean","INTERSECT",EDGE,{"derivedFrom":[makeQuery(id+"F1.opRevolve","SWEPT_FACE",FACE,{"disambiguationData":[OSD([sQuery(id+"F0.wireOp",EDGE,"E3")])]}),makeQuery(id+"F7.opExtrude","SWEPT_FACE",FACE,{"disambiguationData":[OSD([sQuery(id+"F6.wireOp",EDGE,"E25.2.2")])]})]});
            fillet(context, id + "F10", {"entities" : qUnion([Q0, Q1, Q2, Q3, Q4, Q5, Q6, Q7, Q8, Q9, Q10, Q11]), "radius" : 0.3 * mm, "tangentPropagation" : true, "allowEdgeOverflow" : false});
        }
    });
